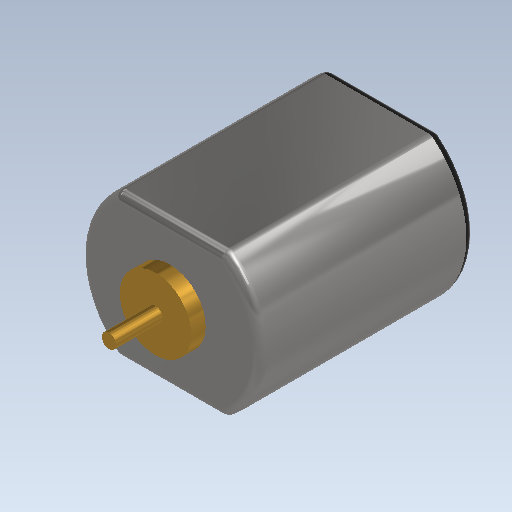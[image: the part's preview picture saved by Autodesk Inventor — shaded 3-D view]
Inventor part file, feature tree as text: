
AUTODESK INVENTOR PART (.ipt)
format: ipt  version: 2020 (Build 240168000, 168)  size: 183,296 bytes
history: native  units: mm
features: sketch x2, other x1, revolve x1, extrude x1, fillet x1
ambient origin geometry x8: Origin, YZ Plane, XZ Plane, XY Plane, X Axis, Y Axis, Z Axis, Center Point
bodies: Body1 (feature_tree)
feature tree (6):
  other  "Твердое тело1"
  revolve  "Вращение1"
  extrude  "Выдавливание1"  Depth=16.5mm
  fillet  "Сопряжение1"  Radius=0.8mm
  sketch  "Эскиз1"
  sketch  "Эскиз2"
